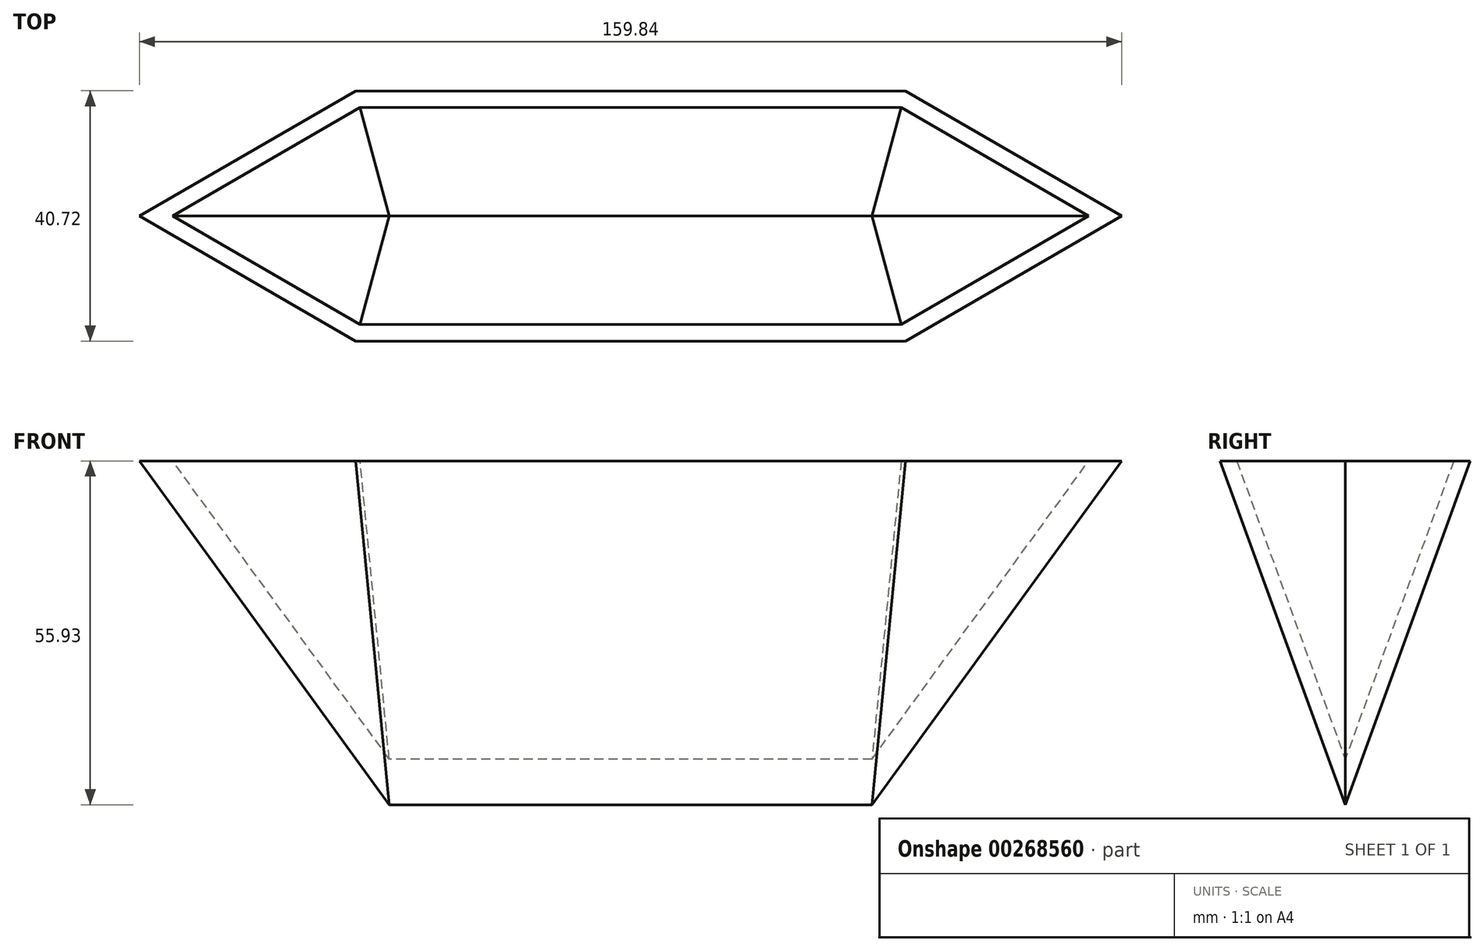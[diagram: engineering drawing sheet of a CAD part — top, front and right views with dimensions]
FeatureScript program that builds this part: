
annotation { "Feature Type Name" : "Feature", "Feature Type Description" : "" }
export const myFeature = defineFeature(function(context is Context, id is Id, definition is map)
    precondition{}
    {
        {
            var Q0;
            Q0=qCreatedBy(makeId("Top.planeOp"),FACE);
            var sketch = newSketch(context, id + "F0", { "sketchPlane" : qUnion([Q0])});
            skLineSegment(sketch, "E0.bottom", {"start": v(44.75, 20.36) * mm, "end": v(-44.75, 20.36) * mm});
            skLineSegment(sketch, "E0.top", {"start": v(44.75, -20.36) * mm, "end": v(-44.75, -20.36) * mm});
            skPoint(sketch, "E0.middle", {"position": v(0, 0) * mm});
            skLineSegment(sketch, "E1", {"start": v(-44.75, 20.36) * mm, "end": v(-79.92, 0) * mm});
            skLineSegment(sketch, "E2", {"start": v(-79.92, 0) * mm, "end": v(-44.75, -20.36) * mm});
            skLineSegment(sketch, "E3", {"start": v(44.75, 20.36) * mm, "end": v(79.92, 0) * mm});
            skLineSegment(sketch, "E4", {"start": v(79.92, 0) * mm, "end": v(44.75, -20.36) * mm});
            skSolve(sketch);
        }
        {
            var Q0;
            Q0 = qSketchRegion(id + "F0", true);
            extrude(context, id + "F1", {"entities" : qUnion([Q0]), "oppositeDirection" : true, "depth" : 62.23 * mm, "hasDraft" : true, "draftAngle" : 20 * degree, "draftPullDirection" : true});
        }
        {
            var Q0;
            Q0=makeQuery(id+"F1.opExtrude","CAP_FACE",FACE,{"disambiguationData":[OSD([sQuery(id+"F0.wireOp",EDGE,"E0.bottom"),sQuery(id+"F0.wireOp",EDGE,"E0.top"),sQuery(id+"F0.wireOp",EDGE,"E1"),sQuery(id+"F0.wireOp",EDGE,"E2"),sQuery(id+"F0.wireOp",EDGE,"E3"),sQuery(id+"F0.wireOp",EDGE,"E4")])],"isStart":true});
            shell(context, id + "F2", {"entities" : qUnion([Q0]), "thickness" : 2.54 * mm});
        }
    });
